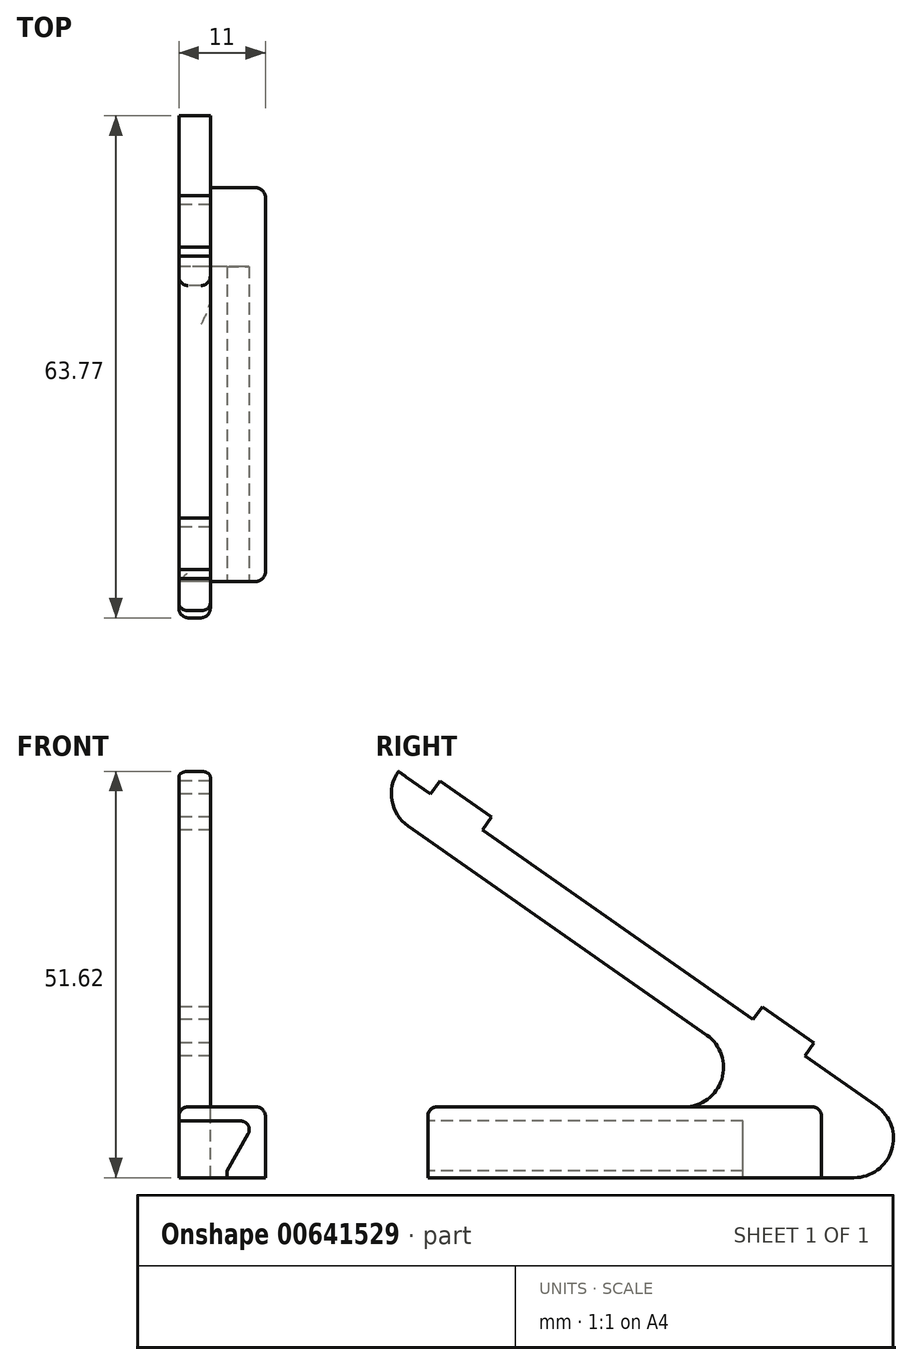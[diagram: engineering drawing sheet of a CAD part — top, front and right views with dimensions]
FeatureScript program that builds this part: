
annotation { "Feature Type Name" : "Feature", "Feature Type Description" : "" }
export const myFeature = defineFeature(function(context is Context, id is Id, definition is map)
    precondition{}
    {
        {
            var Q0;
            Q0=qCreatedBy(makeId("Right.planeOp"),FACE);
            var sketch = newSketch(context, id + "F0", { "sketchPlane" : qUnion([Q0])});
            skLineSegment(sketch, "E0", {"start": v(-40, 0) * mm, "end": v(14.14, 0) * mm});
            skLineSegment(sketch, "E1", {"start": v(17, 9.1) * mm, "end": v(-43.72, 51.62) * mm});
            skLineSegment(sketch, "E2.0", {"start": v(-40, 9) * mm, "end": v(-7.43, 9) * mm});
            skLineSegment(sketch, "E3", {"start": v(-40, 0) * mm, "end": v(-40, 9) * mm});
            skLineSegment(sketch, "E4.0", {"start": v(-4.56, 18.1) * mm, "end": v(-42.5, 44.66) * mm});
            skArc(sketch, "E5.filletArc", {"start": v(-7.43, 9) * mm, "mid": v(-2.66, 12.5) * mm, "end": v(-4.56, 18.1) * mm});
            skPoint(sketch, "E6.visualSharp", {"position": v(30, 0) * mm});
            skArc(sketch, "E6.filletArc", {"start": v(14.14, 0) * mm, "mid": v(18.91, 3.5) * mm, "end": v(17, 9.1) * mm});
            skLineSegment(sketch, "E7", {"start": v(-34.93, 55.46) * mm, "end": v(-39.63, 48.75) * mm, "construction": true});
            skArc(sketch, "E8", {"start": v(-43.72, 51.62) * mm, "mid": v(-44.55, 47.89) * mm, "end": v(-42.5, 44.66) * mm});
            skLineSegment(sketch, "E9", {"start": v(-39.63, 48.75) * mm, "end": v(-38.48, 50.4) * mm});
            skLineSegment(sketch, "E10", {"start": v(-38.48, 50.4) * mm, "end": v(-31.93, 45.8) * mm});
            skLineSegment(sketch, "E11", {"start": v(-31.93, 45.8) * mm, "end": v(-33.07, 44.17) * mm});
            skLineSegment(sketch, "E12", {"start": v(1.33, 20.08) * mm, "end": v(2.48, 21.71) * mm});
            skLineSegment(sketch, "E13", {"start": v(2.48, 21.71) * mm, "end": v(9.03, 17.12) * mm});
            skLineSegment(sketch, "E14", {"start": v(9.03, 17.12) * mm, "end": v(7.88, 15.49) * mm});
            skSolve(sketch);
        }
        {
            var Q0;
            Q0=makeQuery(id+"F0.imprint","IMPRINT",FACE,{"disambiguationData":[TD([[makeQuery(id+"F0.imprint","IMPRINT",EDGE,{"derivedFrom":sQuery(id+"F0.wireOp",EDGE,"E0")}),1.0]])]});
            var Q1;
            {var subQ0=sQuery(id+"F0.wireOp",EDGE,"E9");Q1=makeQuery(id+"F0.imprint","IMPRINT",FACE,{"disambiguationData":[TD([[makeQuery(id+"F0.imprint","IMPRINT",EDGE,{"derivedFrom":subQ0}),-1.0]])]});}
            var Q2;
            {var subQ0=sQuery(id+"F0.wireOp",EDGE,"E12");Q2=makeQuery(id+"F0.imprint","IMPRINT",FACE,{"disambiguationData":[TD([[makeQuery(id+"F0.imprint","IMPRINT",EDGE,{"derivedFrom":subQ0}),-1.0]])]});}
            extrude(context, id + "F1", {"entities" : qUnion([Q0, Q1, Q2]), "endBound" : BoundingType.SYMMETRIC, "depth" : 4 * mm, "offsetDistance" : 25 * mm});
        }
        {
            var Q0;
            Q0=makeQuery(id+"F1.opExtrude","CAP_FACE",FACE,{"disambiguationData":[OSD([sQuery(id+"F0.wireOp",EDGE,"E0"),sQuery(id+"F0.wireOp",EDGE,"E1"),sQuery(id+"F0.wireOp",EDGE,"E2.0"),sQuery(id+"F0.wireOp",EDGE,"E3"),sQuery(id+"F0.wireOp",EDGE,"E4.0"),sQuery(id+"F0.wireOp",EDGE,"E5.filletArc"),sQuery(id+"F0.wireOp",EDGE,"E6.filletArc"),sQuery(id+"F0.wireOp",EDGE,"E8")])],"isStart":false});
            var sketch = newSketch(context, id + "F2", { "sketchPlane" : qUnion([Q0])});
            skPoint(sketch, "E15.0", {"position": v(-40, 0) * mm});
            skPoint(sketch, "E16.0", {"position": v(-40, 9) * mm});
            skLineSegment(sketch, "E17.bottom", {"start": v(-40, 0) * mm, "end": v(10, 0) * mm});
            skLineSegment(sketch, "E17.top", {"start": v(-40, 9) * mm, "end": v(10, 9) * mm});
            skLineSegment(sketch, "E17.left", {"start": v(-40, 0) * mm, "end": v(-40, 9) * mm});
            skLineSegment(sketch, "E17.right", {"start": v(10, 0) * mm, "end": v(10, 9) * mm});
            skSolve(sketch);
        }
        {
            var Q0;
            Q0=makeQuery(id+"F2.imprint","IMPRINT",FACE,{"disambiguationData":[TD([[makeQuery(id+"F2.imprint","IMPRINT",EDGE,{"derivedFrom":sQuery(id+"F2.wireOp",EDGE,"E17.bottom")}),1.0]])]});
            extrude(context, id + "F3", {"entities" : qUnion([Q0]), "operationType" : NewBodyOperationType.ADD, "depth" : 7 * mm, "offsetDistance" : 25 * mm});
        }
        {
            var Q0;
            {var subQ0=sQuery(id+"F2.wireOp",EDGE,"E17.left");Q0=makeQuery(id+"FFfjbwOKtz71IE1_1.1.F3.boolean.opBoolean","MERGE",FACE,{"derivedFrom":[makeQuery(id+"F3.boolean.opBoolean","MERGE",FACE,{"derivedFrom":[makeQuery(id+"F1.opExtrude","SWEPT_FACE",FACE,{"disambiguationData":[OSD([sQuery(id+"F0.wireOp",EDGE,"E3")])]}),makeQuery(id+"F3.opExtrude","SWEPT_FACE",FACE,{"disambiguationData":[OSD([subQ0])]})]}),makeQuery(id+"FFfjbwOKtz71IE1_1.1.F3.opExtrude","SWEPT_FACE",FACE,{"disambiguationData":[OSD([subQ0])]})]});}
            var sketch = newSketch(context, id + "F4", { "sketchPlane" : qUnion([Q0])});
            skLineSegment(sketch, "E18", {"start": v(4.1, 0.87) * mm, "end": v(6.8, 5.55) * mm});
            skLineSegment(sketch, "E19", {"start": v(5.85, 7.2) * mm, "end": v(-5.85, 7.2) * mm});
            skLineSegment(sketch, "E20", {"start": v(-6.8, 5.55) * mm, "end": v(-4.1, 0.87) * mm});
            skPoint(sketch, "E21.orphan", {"position": v(-9, 0) * mm});
            skPoint(sketch, "E22.orphan", {"position": v(9, 0) * mm});
            skPoint(sketch, "E23.visualSharp", {"position": v(-7.76, 7.2) * mm});
            skArc(sketch, "E23.filletArc", {"start": v(-5.85, 7.2) * mm, "mid": v(-6.8, 6.65) * mm, "end": v(-6.8, 5.55) * mm});
            skPoint(sketch, "E24.visualSharp", {"position": v(7.76, 7.2) * mm});
            skArc(sketch, "E24.filletArc", {"start": v(6.8, 5.55) * mm, "mid": v(6.8, 6.65) * mm, "end": v(5.85, 7.2) * mm});
            skLineSegment(sketch, "E25", {"start": v(-4.1, 0) * mm, "end": v(-4.1, 0.87) * mm});
            skLineSegment(sketch, "E26.MirrorCS", {"start": v(4.1, 0) * mm, "end": v(4.1, 0.87) * mm});
            skLineSegment(sketch, "E27", {"start": v(-4.1, 0) * mm, "end": v(4.1, 0) * mm});
            skSolve(sketch);
        }
        {
            var Q0;
            Q0=makeQuery(id+"F4.imprint","IMPRINT",FACE,{"disambiguationData":[TD([[makeQuery(id+"F4.imprint","IMPRINT",EDGE,{"derivedFrom":sQuery(id+"F4.wireOp",EDGE,"E18")}),1.0]])]});
            extrude(context, id + "F5", {"entities" : qUnion([Q0]), "operationType" : NewBodyOperationType.REMOVE, "oppositeDirection" : true, "depth" : 40 * mm, "offsetDistance" : 25 * mm});
        }
        {
            var Q0;
            Q0=makeQuery(id+"FFfjbwOKtz71IE1_1.1.F3.opExtrude","CAP_EDGE",EDGE,{"disambiguationData":[OSD([sQuery(id+"F2.wireOp",EDGE,"E17.top")])],"isStart":false});
            var Q1;
            Q1=makeQuery(id+"F3.opExtrude","CAP_EDGE",EDGE,{"disambiguationData":[OSD([sQuery(id+"F2.wireOp",EDGE,"E17.top")])],"isStart":false});
            var Q2;
            {var subQ0=sQuery(id+"F2.wireOp",EDGE,"E17.left");var subQ1=sQuery(id+"F2.wireOp",EDGE,"E17.top");Q2=makeQuery(id+"FFfjbwOKtz71IE1_1.1.F3.boolean.opBoolean","MERGE",EDGE,{"derivedFrom":[makeQuery(id+"F3.boolean.opBoolean","MERGE",EDGE,{"derivedFrom":[makeQuery(id+"F1.opExtrude","SWEPT_EDGE",EDGE,{"disambiguationData":[OSD([sQuery(id+"F0.wireOp",EDGE,"E2.0"),sQuery(id+"F0.wireOp",EDGE,"E3")])]}),makeQuery(id+"F3.opExtrude","SWEPT_EDGE",EDGE,{"disambiguationData":[OSD([subQ1,subQ0])]})]}),makeQuery(id+"FFfjbwOKtz71IE1_1.1.F3.opExtrude","SWEPT_EDGE",EDGE,{"disambiguationData":[OSD([subQ1,subQ0])]})]});}
            var Q3;
            Q3=makeQuery(id+"F3.opExtrude","CAP_EDGE",EDGE,{"disambiguationData":[OSD([sQuery(id+"F2.wireOp",EDGE,"E17.left")])],"isStart":false});
            var Q4;
            Q4=makeQuery(id+"FFfjbwOKtz71IE1_1.1.F3.opExtrude","CAP_EDGE",EDGE,{"disambiguationData":[OSD([sQuery(id+"F2.wireOp",EDGE,"E17.left")])],"isStart":false});
            var Q5;
            Q5=makeQuery(id+"F3.opExtrude","CAP_EDGE",EDGE,{"disambiguationData":[OSD([sQuery(id+"F2.wireOp",EDGE,"E17.right")])],"isStart":false});
            var Q6;
            Q6=makeQuery(id+"F3.opExtrude","SWEPT_EDGE",EDGE,{"disambiguationData":[OSD([sQuery(id+"F2.wireOp",EDGE,"E17.top"),sQuery(id+"F2.wireOp",EDGE,"E17.right")])]});
            var Q7;
            Q7=makeQuery(id+"F3.opExtrude","CAP_EDGE",EDGE,{"disambiguationData":[OSD([sQuery(id+"F2.wireOp",EDGE,"E17.right")])],"isStart":true});
            var Q8;
            Q8=makeQuery(id+"FFfjbwOKtz71IE1_1.1.F3.opExtrude","CAP_EDGE",EDGE,{"disambiguationData":[OSD([sQuery(id+"F2.wireOp",EDGE,"E17.right")])],"isStart":true});
            var Q9;
            Q9=makeQuery(id+"FFfjbwOKtz71IE1_1.1.F3.opExtrude","SWEPT_EDGE",EDGE,{"disambiguationData":[OSD([sQuery(id+"F2.wireOp",EDGE,"E17.top"),sQuery(id+"F2.wireOp",EDGE,"E17.right")])]});
            var Q10;
            Q10=makeQuery(id+"FFfjbwOKtz71IE1_1.1.F3.opExtrude","CAP_EDGE",EDGE,{"disambiguationData":[OSD([sQuery(id+"F2.wireOp",EDGE,"E17.right")])],"isStart":false});
            var Q11;
            Q11=makeQuery(id+"F1.opExtrude","CAP_EDGE",EDGE,{"disambiguationData":[OSD([sQuery(id+"F0.wireOp",EDGE,"E5.filletArc")])],"isStart":true});
            var Q12;
            Q12=makeQuery(id+"F1.opExtrude","CAP_EDGE",EDGE,{"disambiguationData":[OSD([sQuery(id+"F0.wireOp",EDGE,"E5.filletArc")])],"isStart":false});
            fillet(context, id + "F6", {"entities" : qUnion([Q0, Q1, Q2, Q3, Q4, Q5, Q6, Q7, Q8, Q9, Q10, Q11, Q12]), "radius" : 1.2 * mm, "tangentPropagation" : true, "allowEdgeOverflow" : false});
        }
    });
